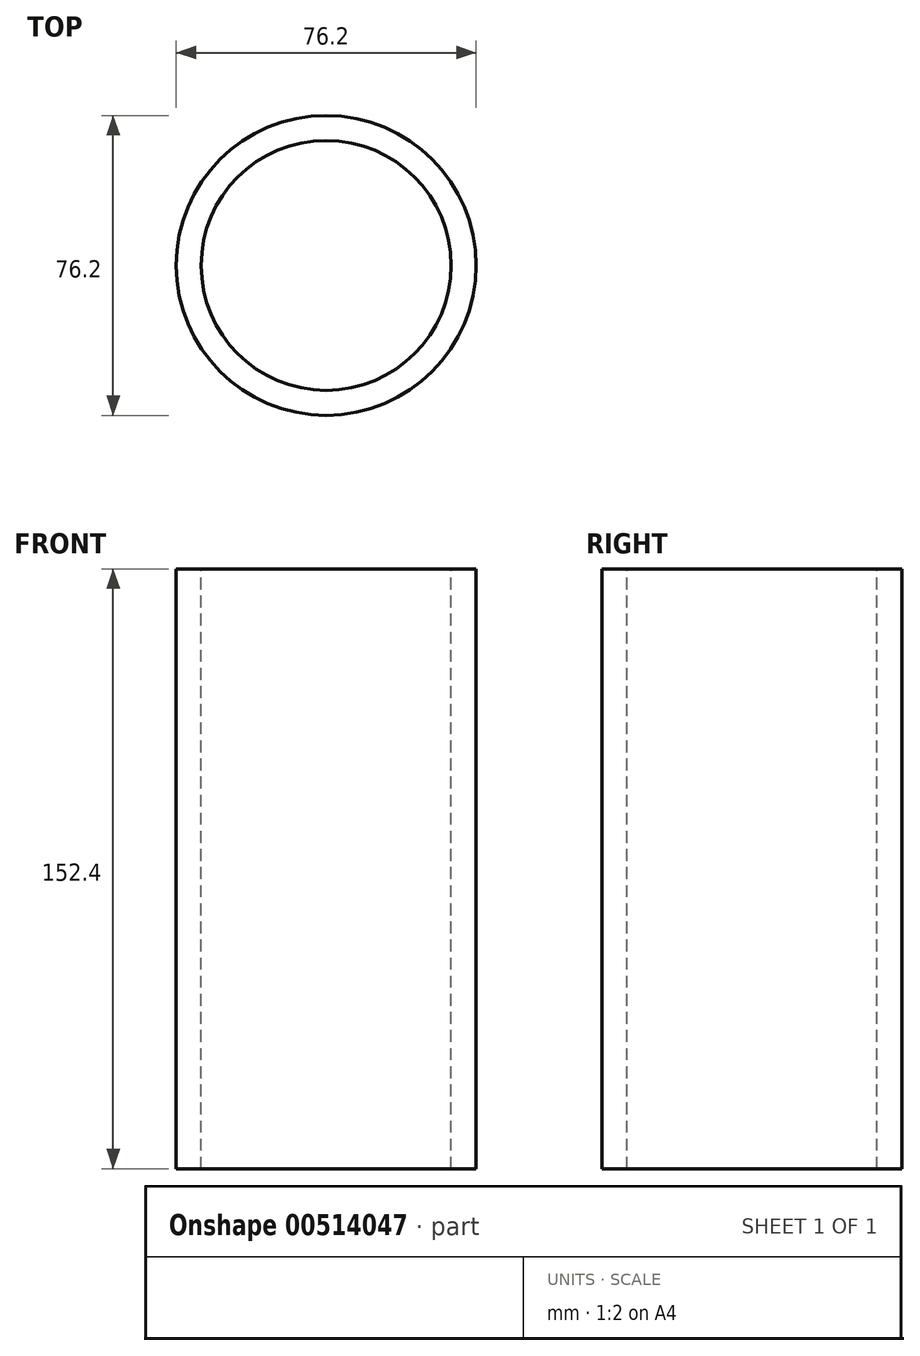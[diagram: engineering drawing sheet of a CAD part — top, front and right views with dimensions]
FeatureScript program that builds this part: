
annotation { "Feature Type Name" : "Feature", "Feature Type Description" : "" }
export const myFeature = defineFeature(function(context is Context, id is Id, definition is map)
    precondition{}
    {
        {
            var Q0;
            Q0=qCreatedBy(makeId("Top.planeOp"),FACE);
            var sketch = newSketch(context, id + "F0", { "sketchPlane" : qUnion([Q0])});
            skCircle(sketch, "E0", {"center": v(0, 0) * mm, "radius": 38.1 * mm});
            skCircle(sketch, "E1.0", {"center": v(0, 0) * mm, "radius": 31.75 * mm});
            skSolve(sketch);
        }
        {
            var Q0;
            Q0 = qSketchRegion(id + "F0", true);
            extrude(context, id + "F1", {"entities" : qUnion([Q0]), "oppositeDirection" : true, "depth" : 152.4 * mm});
        }
    });
